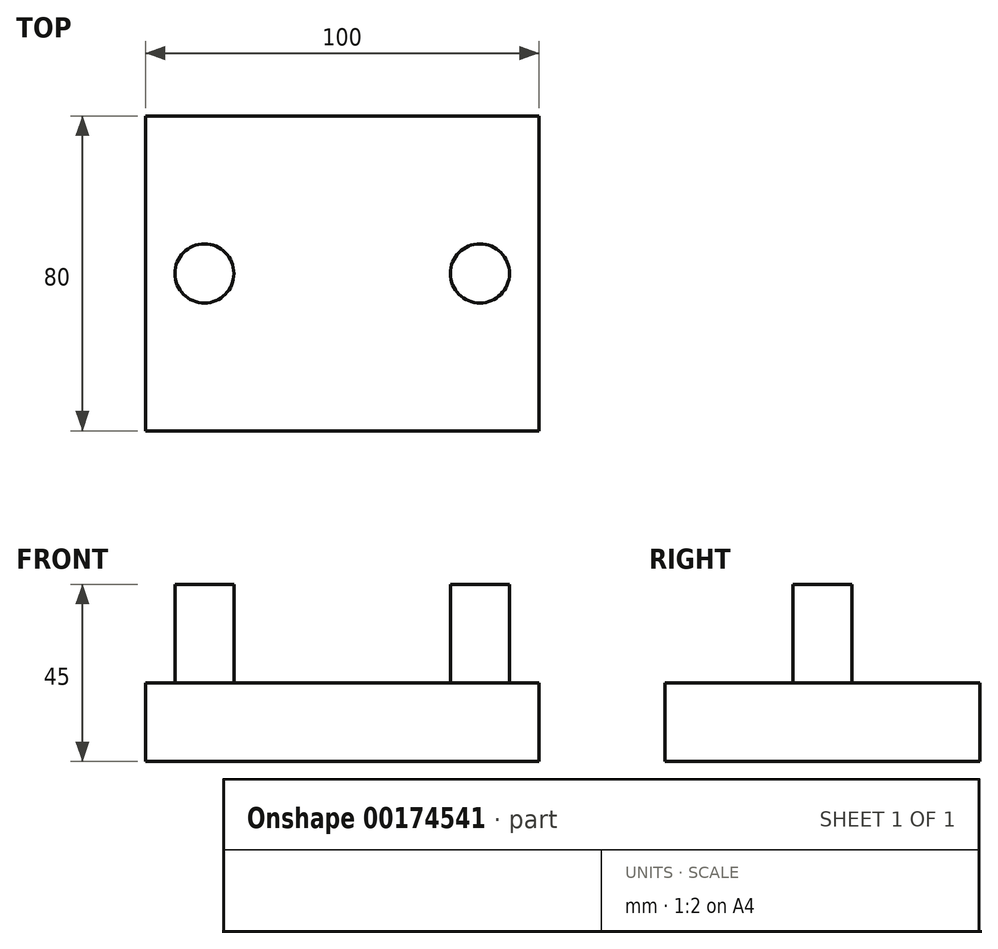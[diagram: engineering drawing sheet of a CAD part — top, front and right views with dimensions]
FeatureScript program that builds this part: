
annotation { "Feature Type Name" : "Feature", "Feature Type Description" : "" }
export const myFeature = defineFeature(function(context is Context, id is Id, definition is map)
    precondition{}
    {
        {
            var Q0;
            Q0=qCreatedBy(makeId("Top.planeOp"),FACE);
            var sketch = newSketch(context, id + "F0", { "sketchPlane" : qUnion([Q0])});
            skLineSegment(sketch, "E0.bottom", {"start": v(-50, 40) * mm, "end": v(50, 40) * mm});
            skLineSegment(sketch, "E0.top", {"start": v(-50, -40) * mm, "end": v(50, -40) * mm});
            skLineSegment(sketch, "E0.left", {"start": v(-50, 40) * mm, "end": v(-50, -40) * mm});
            skLineSegment(sketch, "E0.right", {"start": v(50, 40) * mm, "end": v(50, -40) * mm});
            skLineSegment(sketch, "E1", {"start": v(-55.75, 0) * mm, "end": v(74.2, 0) * mm, "construction": true});
            skLineSegment(sketch, "E2", {"start": v(0, 66.18) * mm, "end": v(0, -57.62) * mm, "construction": true});
            skSolve(sketch);
        }
        {
            var Q0;
            Q0 = qSketchRegion(id + "F0", true);
            extrude(context, id + "F1", {"entities" : qUnion([Q0]), "depth" : 20 * mm});
        }
        {
            var Q0;
            Q0=makeQuery(id+"F1.opExtrude","CAP_FACE",FACE,{"disambiguationData":[OSD([sQuery(id+"F0.wireOp",EDGE,"E0.bottom"),sQuery(id+"F0.wireOp",EDGE,"E0.top"),sQuery(id+"F0.wireOp",EDGE,"E0.left"),sQuery(id+"F0.wireOp",EDGE,"E0.right")])],"isStart":false});
            var sketch = newSketch(context, id + "F2", { "sketchPlane" : qUnion([Q0])});
            skCircle(sketch, "E3", {"center": v(-35, 0) * mm, "radius": 7.5 * mm});
            skCircle(sketch, "E4", {"center": v(35, 0) * mm, "radius": 7.5 * mm});
            skSolve(sketch);
        }
        {
            var Q0;
            Q0 = qSketchRegion(id + "F2", true);
            extrude(context, id + "F3", {"entities" : qUnion([Q0]), "operationType" : NewBodyOperationType.ADD, "depth" : 25 * mm});
        }
    });
